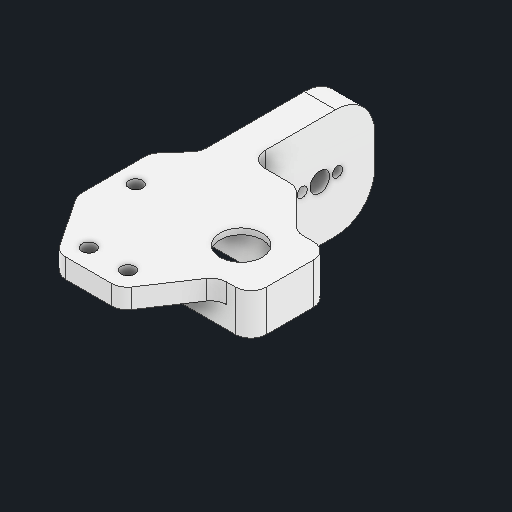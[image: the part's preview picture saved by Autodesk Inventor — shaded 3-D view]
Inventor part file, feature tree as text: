
AUTODESK INVENTOR PART (.ipt)
format: ipt  version: 2023 (Build 270158000, 158)  size: 141,312 bytes
history: native  units: mm
features: fillet x1
ambient origin geometry x8: Origin, YZ Plane, XZ Plane, XY Plane, X Axis, Y Axis, Z Axis, Center Point
bodies: Solid1 (feature_tree)
feature tree (1):
  fillet  "Fillet13"  [1 undecoded]
note: 1 required parameter value undecoded (feature->parameter linkage not recoverable at this tier; creation-order binding heuristic only, values carry confidence <= 0.55)
